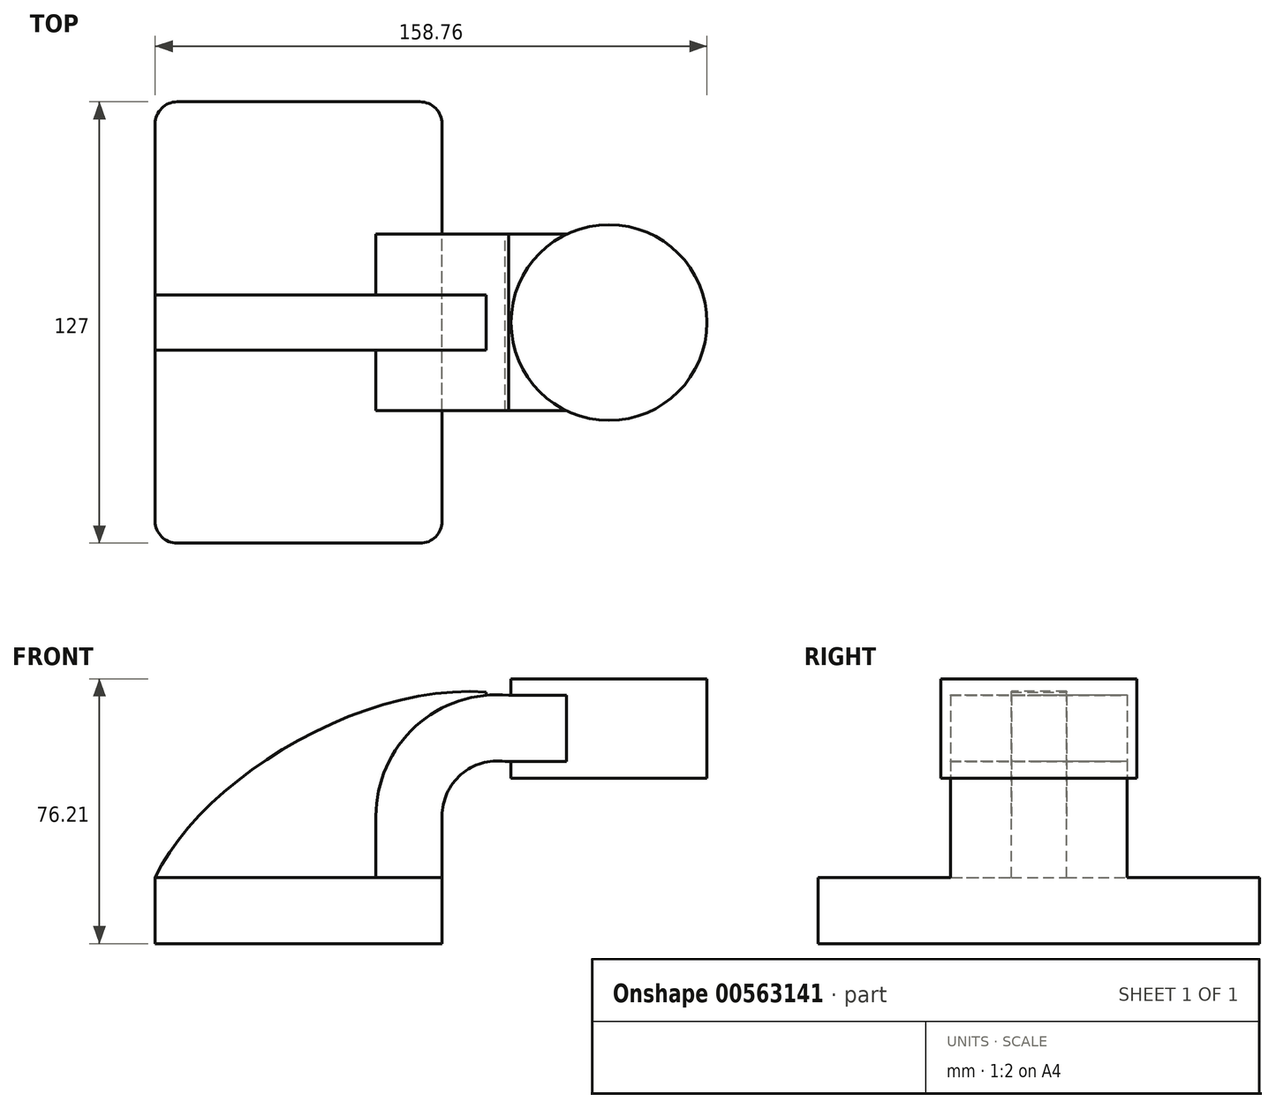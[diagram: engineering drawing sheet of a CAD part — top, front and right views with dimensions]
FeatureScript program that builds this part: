
annotation { "Feature Type Name" : "Feature", "Feature Type Description" : "" }
export const myFeature = defineFeature(function(context is Context, id is Id, definition is map)
    precondition{}
    {
        {
            var Q0;
            Q0=qCreatedBy(makeId("Front.planeOp"),FACE);
            var sketch = newSketch(context, id + "F0", { "sketchPlane" : qUnion([Q0])});
            skLineSegment(sketch, "E0.bottom", {"start": v(-41.28, -9.53) * mm, "end": v(41.28, -9.53) * mm});
            skLineSegment(sketch, "E0.top", {"start": v(-41.28, 9.52) * mm, "end": v(41.28, 9.52) * mm});
            skLineSegment(sketch, "E0.left", {"start": v(-41.27, -9.53) * mm, "end": v(-41.28, 9.52) * mm});
            skLineSegment(sketch, "E0.right", {"start": v(41.28, -9.53) * mm, "end": v(41.28, 9.52) * mm});
            skPoint(sketch, "E0.middle", {"position": v(0, 0) * mm});
            skLineSegment(sketch, "E1.bottom", {"start": v(53.97, 38.1) * mm, "end": v(117.47, 38.1) * mm});
            skLineSegment(sketch, "E1.top", {"start": v(53.97, 66.67) * mm, "end": v(117.47, 66.67) * mm});
            skLineSegment(sketch, "E1.left", {"start": v(53.98, 38.1) * mm, "end": v(53.97, 66.67) * mm});
            skLineSegment(sketch, "E1.right", {"start": v(117.47, 38.1) * mm, "end": v(117.47, 66.67) * mm});
            skPoint(sketch, "E1.middle", {"position": v(85.72, 52.39) * mm});
            skLineSegment(sketch, "E2", {"start": v(41.27, 9.52) * mm, "end": v(41.27, 27.16) * mm});
            skArc(sketch, "E3", {"start": v(41.28, 27.16) * mm, "mid": v(46.74, 39.14) * mm, "end": v(59.37, 42.88) * mm});
            skLineSegment(sketch, "E4", {"start": v(59.37, 42.88) * mm, "end": v(89.3, 42.88) * mm});
            skLineSegment(sketch, "E5.0", {"start": v(60.45, 61.93) * mm, "end": v(95.65, 61.93) * mm});
            skArc(sketch, "E5.1", {"start": v(22.23, 27.16) * mm, "mid": v(33.65, 53) * mm, "end": v(60.45, 61.93) * mm});
            skLineSegment(sketch, "E5.2", {"start": v(22.22, 9.52) * mm, "end": v(22.22, 27.16) * mm});
            skLineSegment(sketch, "E6", {"start": v(89.3, 38.1) * mm, "end": v(89.3, 66.67) * mm});
            skFitSpline(sketch, "E7", {"points": [v(-41.28, 9.53) * mm, v(60.45, 61.93) * mm], "startDerivative": vector(41.31, 87.77) * mm, "endDerivative": vector(111.38, -21.72) * mm});
            skSolve(sketch);
        }
        {
            var Q0;
            Q0=makeQuery(id+"F0.imprint","IMPRINT",FACE,{"disambiguationData":[TD([[makeQuery(id+"F0.imprint","IMPRINT",EDGE,{"derivedFrom":sQuery(id+"F0.wireOp",EDGE,"E0.bottom")}),1.0]])]});
            extrude(context, id + "F1", {"entities" : qUnion([Q0]), "endBound" : BoundingType.SYMMETRIC, "depth" : 127 * mm, "offsetDistance" : 25.4 * mm});
        }
        {
            var Q0;
            {var subQ0=sQuery(id+"F0.wireOp",EDGE,"E2");Q0=makeQuery(id+"F0.imprint","IMPRINT",FACE,{"disambiguationData":[TD([[makeQuery(id+"F0.imprint","IMPRINT",EDGE,{"derivedFrom":subQ0}),1.0]])]});}
            extrude(context, id + "F2", {"entities" : qUnion([Q0]), "operationType" : NewBodyOperationType.ADD, "endBound" : BoundingType.SYMMETRIC, "depth" : 50.8 * mm, "offsetDistance" : 25.4 * mm});
        }
        {
            var Q0;
            {var subQ0=sQuery(id+"F0.wireOp",EDGE,"E5.2");Q0=makeQuery(id+"F0.imprint","IMPRINT",FACE,{"disambiguationData":[TD([[makeQuery(id+"F0.imprint","IMPRINT",EDGE,{"derivedFrom":subQ0}),1.0]])]});}
            extrude(context, id + "F3", {"entities" : qUnion([Q0]), "operationType" : NewBodyOperationType.ADD, "endBound" : BoundingType.SYMMETRIC, "depth" : 15.88 * mm, "offsetDistance" : 25.4 * mm});
        }
        {
            var Q0;
            {var subQ0=sQuery(id+"F0.wireOp",EDGE,"E5.0");Q0=makeQuery(id+"F0.imprint","IMPRINT",FACE,{"disambiguationData":[TD([[makeQuery(id+"F0.imprint","IMPRINT",EDGE,{"derivedFrom":subQ0}),-1.0]])]});}
            extrude(context, id + "F4", {"entities" : qUnion([Q0]), "operationType" : NewBodyOperationType.ADD, "endBound" : BoundingType.SYMMETRIC, "depth" : 50.8 * mm, "offsetDistance" : 25.4 * mm});
        }
        {
            var Q0;
            {var subQ4=sQuery(id+"F0.wireOp",EDGE,"E1.right");Q0=makeQuery(id+"F0.imprint","IMPRINT",FACE,{"disambiguationData":[TD([[makeQuery(id+"F0.imprint","IMPRINT",EDGE,{"derivedFrom":subQ4}),1.0]])]});}
            var Q1;
            Q1=sQuery(id+"F0.wireOp",EDGE,"E6");
            revolve(context, id + "F5", {"operationType" : NewBodyOperationType.ADD, "entities" : qUnion([Q0]), "axis" : qUnion([Q1]), "revolveType" : RevolveType.FULL});
        }
        {
            var Q0;
            Q0=makeQuery(id+"F1.opExtrude","CAP_EDGE",EDGE,{"disambiguationData":[OSD([sQuery(id+"F0.wireOp",EDGE,"E0.right")])],"isStart":false});
            var Q1;
            Q1=makeQuery(id+"F1.opExtrude","CAP_EDGE",EDGE,{"disambiguationData":[OSD([sQuery(id+"F0.wireOp",EDGE,"E0.left")])],"isStart":false});
            var Q2;
            Q2=makeQuery(id+"F1.opExtrude","CAP_EDGE",EDGE,{"disambiguationData":[OSD([sQuery(id+"F0.wireOp",EDGE,"E0.left")])],"isStart":true});
            var Q3;
            Q3=makeQuery(id+"F1.opExtrude","CAP_EDGE",EDGE,{"disambiguationData":[OSD([sQuery(id+"F0.wireOp",EDGE,"E0.right")])],"isStart":true});
            fillet(context, id + "F6", {"entities" : qUnion([Q0, Q1, Q2, Q3]), "radius" : 6.35 * mm, "tangentPropagation" : true, "allowEdgeOverflow" : false});
        }
    });
